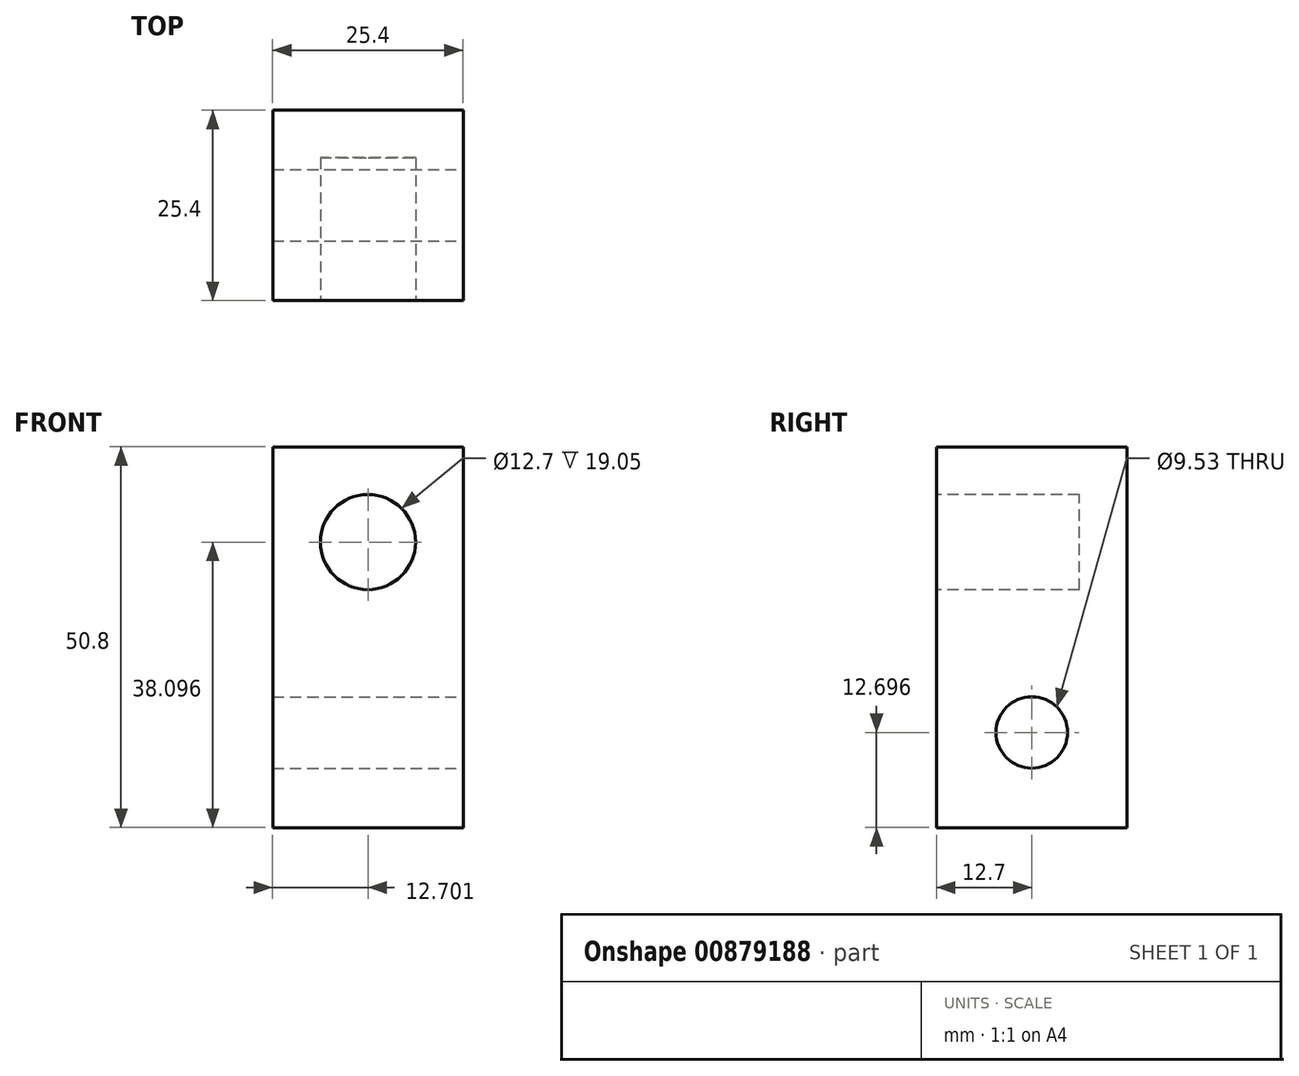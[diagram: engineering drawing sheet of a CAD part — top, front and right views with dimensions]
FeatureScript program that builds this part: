
annotation { "Feature Type Name" : "Feature", "Feature Type Description" : "" }
export const myFeature = defineFeature(function(context is Context, id is Id, definition is map)
    precondition{}
    {
        {
            var Q0;
            Q0=qCreatedBy(makeId("Front.planeOp"),FACE);
            var sketch = newSketch(context, id + "F0", { "sketchPlane" : qUnion([Q0])});
            skLineSegment(sketch, "E0.bottom", {"start": v(-25.66, -41.08) * mm, "end": v(-0.26, -41.08) * mm});
            skLineSegment(sketch, "E0.top", {"start": v(-25.66, 9.72) * mm, "end": v(-0.26, 9.72) * mm});
            skLineSegment(sketch, "E0.left", {"start": v(-25.66, -41.08) * mm, "end": v(-25.66, 9.72) * mm});
            skLineSegment(sketch, "E0.right", {"start": v(-0.26, -41.08) * mm, "end": v(-0.26, 9.72) * mm});
            skSolve(sketch);
        }
        {
            var Q0;
            Q0=qSketchRegion(id+"F0",true);
            extrude(context, id + "F1", {"entities" : qUnion([Q0]), "depth" : 25.4 * mm, "offsetDistance" : 25.4 * mm});
        }
        {
            var Q0;
            Q0=makeQuery(id+"F1.opExtrude","CAP_FACE",FACE,{"disambiguationData":[OSD([sQuery(id+"F0.wireOp",EDGE,"E0.bottom"),sQuery(id+"F0.wireOp",EDGE,"E0.top"),sQuery(id+"F0.wireOp",EDGE,"E0.left"),sQuery(id+"F0.wireOp",EDGE,"E0.right")])],"isStart":false});
            var sketch = newSketch(context, id + "F2", { "sketchPlane" : qUnion([Q0])});
            skCircle(sketch, "E1", {"center": v(-12.96, -2.98) * mm, "radius": 6.35 * mm});
            skSolve(sketch);
        }
        {
            var Q0;
            Q0=qSketchRegion(id+"F2",true);
            extrude(context, id + "F3", {"entities" : qUnion([Q0]), "operationType" : NewBodyOperationType.REMOVE, "oppositeDirection" : true, "depth" : 19.05 * mm, "offsetDistance" : 25.4 * mm});
        }
        {
            var Q0;
            Q0=makeQuery(id+"F1.opExtrude","SWEPT_FACE",FACE,{"disambiguationData":[OSD([sQuery(id+"F0.wireOp",EDGE,"E0.right")])]});
            var sketch = newSketch(context, id + "F4", { "sketchPlane" : qUnion([Q0])});
            skCircle(sketch, "E2", {"center": v(-12.7, -28.38) * mm, "radius": 4.76 * mm});
            skSolve(sketch);
        }
        {
            var Q0;
            Q0=qSketchRegion(id+"F4",true);
            extrude(context, id + "F5", {"entities" : qUnion([Q0]), "operationType" : NewBodyOperationType.REMOVE, "oppositeDirection" : true, "depth" : 25.4 * mm, "offsetDistance" : 25.4 * mm});
        }
    });
